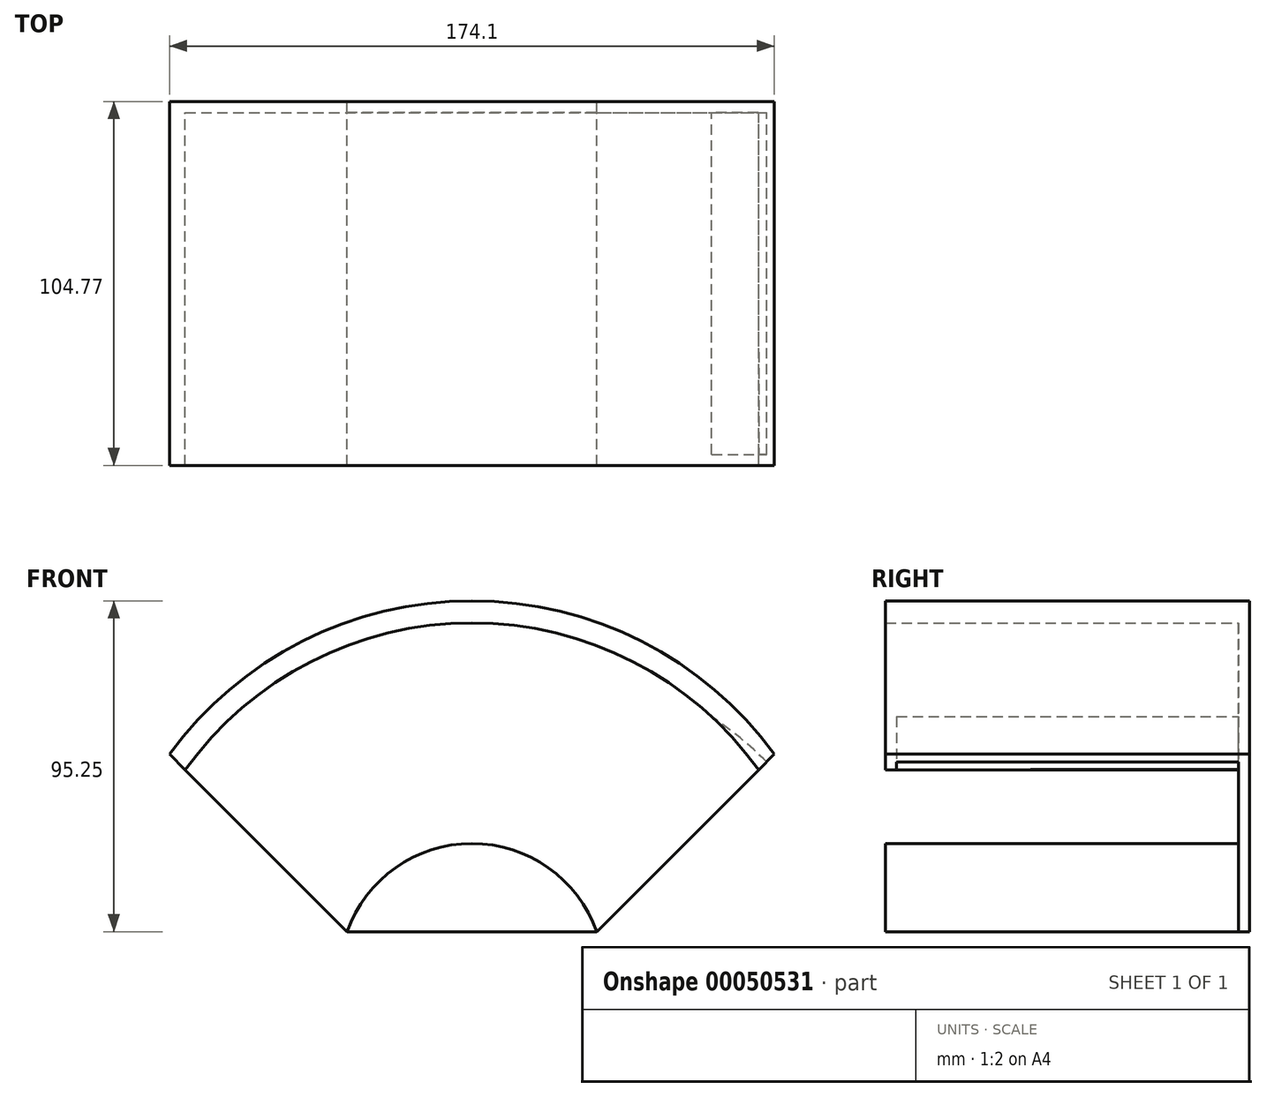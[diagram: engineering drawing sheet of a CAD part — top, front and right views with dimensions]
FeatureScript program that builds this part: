
annotation { "Feature Type Name" : "Feature", "Feature Type Description" : "" }
export const myFeature = defineFeature(function(context is Context, id is Id, definition is map)
    precondition{}
    {
        {
            var Q0;
            Q0=qCreatedBy(makeId("Front.planeOp"),FACE);
            var sketch = newSketch(context, id + "F0", { "sketchPlane" : qUnion([Q0])});
            skArc(sketch, "E0", {"start": v(82.5, 59.29) * mm, "mid": v(0, 101.6) * mm, "end": v(-82.5, 59.29) * mm});
            skArc(sketch, "E1", {"start": v(35.92, 12.7) * mm, "mid": v(0, 38.1) * mm, "end": v(-35.92, 12.7) * mm});
            skLineSegment(sketch, "E2", {"start": v(-87.05, 63.83) * mm, "end": v(-35.92, 12.7) * mm});
            skLineSegment(sketch, "E3", {"start": v(-35.92, 12.7) * mm, "end": v(35.92, 12.7) * mm});
            skLineSegment(sketch, "E4", {"start": v(35.92, 12.7) * mm, "end": v(87.05, 63.83) * mm});
            skLineSegment(sketch, "E5", {"start": v(0, 0) * mm, "end": v(0, 101.6) * mm});
            skArc(sketch, "E6.0", {"start": v(87.66, 63) * mm, "mid": v(0.52, 107.95) * mm, "end": v(-87.05, 63.83) * mm});
            skSolve(sketch);
        }
        {
            var Q0;
            {var subQ0=sQuery(id+"F0.wireOp",EDGE,"E3");var subQ3=sQuery(id+"F0.wireOp",EDGE,"E5");var subQ5=makeQuery(id+"F0.imprint","INTERSECT",VERTEX,{"derivedFrom":[subQ0,subQ3]});Q0=makeQuery(id+"F0.imprint","IMPRINT",FACE,{"disambiguationData":[TD([[makeQuery(id+"F0.imprint","IMPRINT",EDGE,{"disambiguationData":[TD([[subQ5,-1.0]])],"derivedFrom":subQ3}),-1.0]])]});}
            var Q1;
            {var subQ0=sQuery(id+"F0.wireOp",EDGE,"E3");var subQ3=sQuery(id+"F0.wireOp",EDGE,"E5");var subQ5=makeQuery(id+"F0.imprint","INTERSECT",VERTEX,{"derivedFrom":[subQ0,subQ3]});Q1=makeQuery(id+"F0.imprint","IMPRINT",FACE,{"disambiguationData":[TD([[makeQuery(id+"F0.imprint","IMPRINT",EDGE,{"disambiguationData":[TD([[subQ5,-1.0]])],"derivedFrom":subQ3}),1.0]])]});}
            var Q2;
            {var subQ0=sQuery(id+"F0.wireOp",EDGE,"E4");var subQ1=sQuery(id+"F0.wireOp",EDGE,"E0");var subQ2=makeQuery(id+"F0.imprint","INTERSECT",VERTEX,{"derivedFrom":[subQ1,subQ0]});Q2=makeQuery(id+"F0.imprint","IMPRINT",FACE,{"disambiguationData":[TD([[makeQuery(id+"F0.imprint","IMPRINT",EDGE,{"disambiguationData":[TD([[subQ2,-1.0]])],"derivedFrom":subQ1}),-1.0]])]});}
            extrude(context, id + "F1", {"entities" : qUnion([Q0, Q1, Q2]), "depth" : 104.77 * mm});
        }
        {
            var Q0;
            {var subQ0=sQuery(id+"F0.wireOp",EDGE,"E2");var subQ1=sQuery(id+"F0.wireOp",EDGE,"E0");var subQ2=makeQuery(id+"F0.imprint","INTERSECT",VERTEX,{"derivedFrom":[subQ1,subQ0]});Q0=makeQuery(id+"F0.imprint","IMPRINT",FACE,{"disambiguationData":[TD([[makeQuery(id+"F0.imprint","IMPRINT",EDGE,{"disambiguationData":[TD([[subQ2,1.0]])],"derivedFrom":subQ1}),1.0]])]});}
            var Q1;
            {var subQ0=sQuery(id+"F0.wireOp",EDGE,"E4");var subQ1=sQuery(id+"F0.wireOp",EDGE,"E0");var subQ2=makeQuery(id+"F0.imprint","INTERSECT",VERTEX,{"derivedFrom":[subQ1,subQ0]});Q1=makeQuery(id+"F0.imprint","IMPRINT",FACE,{"disambiguationData":[TD([[makeQuery(id+"F0.imprint","IMPRINT",EDGE,{"disambiguationData":[TD([[subQ2,-1.0]])],"derivedFrom":subQ1}),1.0]])]});}
            extrude(context, id + "F2", {"entities" : qUnion([Q0, Q1]), "operationType" : NewBodyOperationType.ADD, "depth" : 3.17 * mm});
        }
        {
            var Q0;
            {var subQ0=sQuery(id+"F0.wireOp",EDGE,"E4");Q0=makeQuery(id+"F2.boolean.opBoolean","MERGE",FACE,{"derivedFrom":[makeQuery(id+"F1.opExtrude","SWEPT_FACE",FACE,{"disambiguationData":[OSD([subQ0])]}),makeQuery(id+"F2.opExtrude","SWEPT_FACE",FACE,{"disambiguationData":[OSD([subQ0])]})]});}
            cPlane(context, id + "F3", {"entities" : qUnion([Q0]), "cplaneType" : CPlaneType.OFFSET, "offset" : 0 * mm, "width" : 152.4 * mm, "height" : 152.4 * mm});
        }
        {
            var Q0;
            Q0=qCreatedBy(id+"F3.planeOp",FACE);
            var sketch = newSketch(context, id + "F4", { "sketchPlane" : qUnion([Q0])});
            skLineSegment(sketch, "E7", {"start": v(-101.6, 100.26) * mm, "end": v(-101.6, 103.52) * mm});
            skLineSegment(sketch, "E8", {"start": v(-101.6, 103.52) * mm, "end": v(-3.17, 103.52) * mm});
            skLineSegment(sketch, "E9", {"start": v(-3.17, 103.52) * mm, "end": v(-3.17, 100.28) * mm});
            skLineSegment(sketch, "E10", {"start": v(-99.1, -1.34) * mm, "end": v(4.7, -1.34) * mm});
            skLineSegment(sketch, "E11", {"start": v(-101.6, 100.26) * mm, "end": v(-3.17, 100.28) * mm});
            skSolve(sketch);
        }
        {
            var Q0;
            Q0=makeQuery(id+"F4.imprint","IMPRINT",FACE,{"disambiguationData":[TD([[makeQuery(id+"F4.imprint","IMPRINT",EDGE,{"derivedFrom":sQuery(id+"F4.wireOp",EDGE,"E7")}),-1.0]])]});
            var Q1;
            Q1=sQuery(id+"F4.wireOp",EDGE,"E10");
            revolve(context, id + "F5", {"operationType" : NewBodyOperationType.REMOVE, "entities" : qUnion([Q0]), "axis" : qUnion([Q1]), "revolveType" : RevolveType.FULL, "oppositeDirection" : true});
        }
    });
